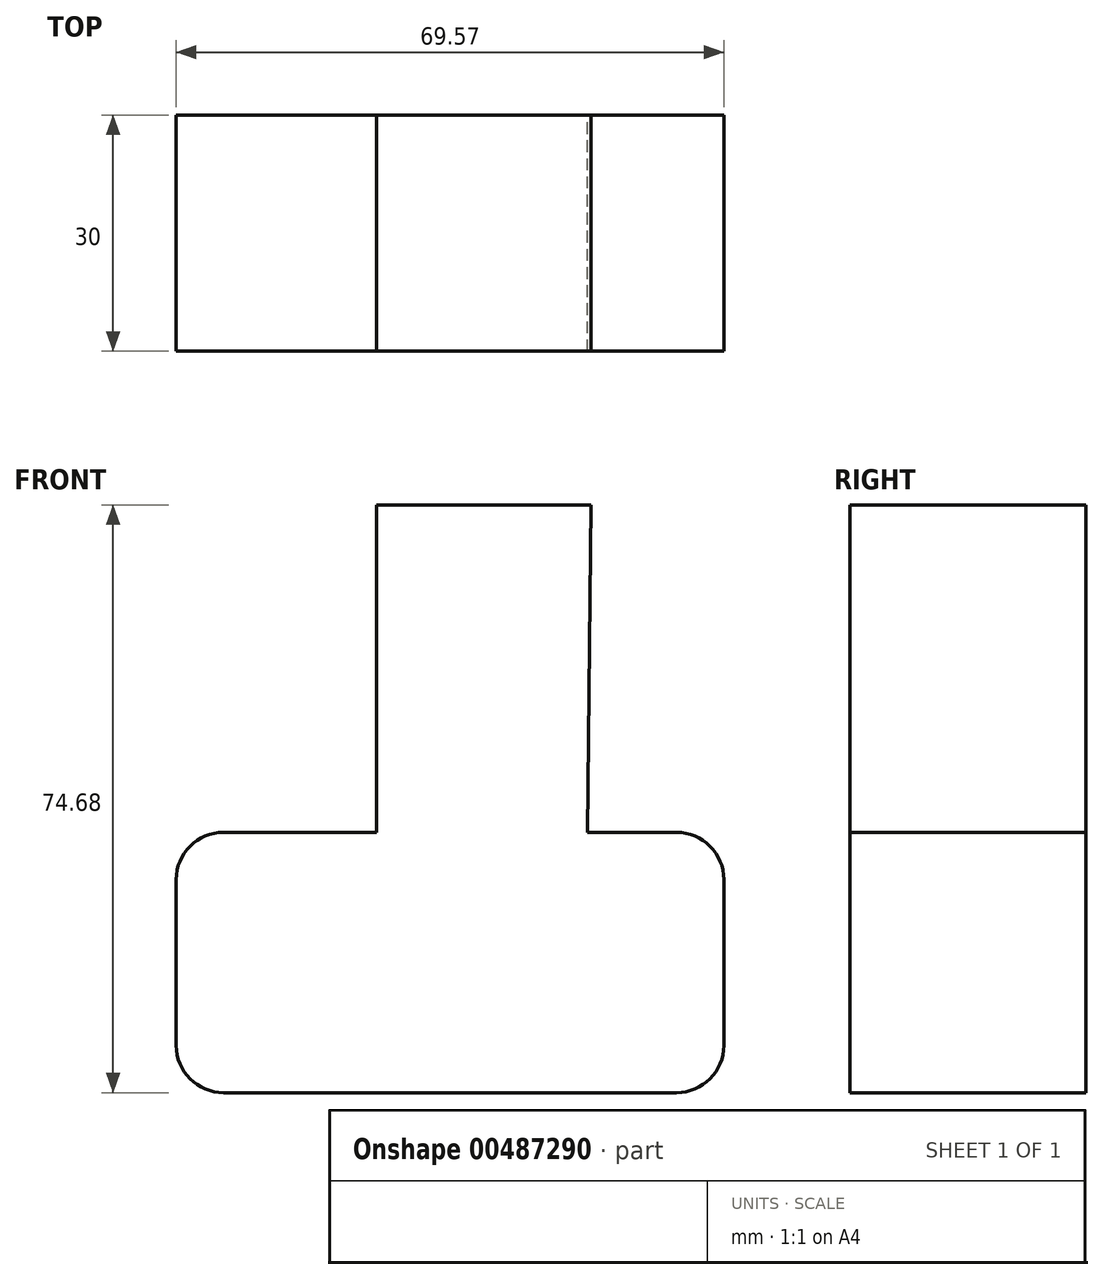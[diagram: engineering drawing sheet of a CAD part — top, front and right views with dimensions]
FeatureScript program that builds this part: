
annotation { "Feature Type Name" : "Feature", "Feature Type Description" : "" }
export const myFeature = defineFeature(function(context is Context, id is Id, definition is map)
    precondition{}
    {
        {
            var Q0;
            Q0=qCreatedBy(makeId("Front.planeOp"),FACE);
            var sketch = newSketch(context, id + "F0", { "sketchPlane" : qUnion([Q0])});
            skLineSegment(sketch, "E0", {"start": v(-14.74, -17.73) * mm, "end": v(42.83, -17.73) * mm});
            skLineSegment(sketch, "E1", {"start": v(48.83, -11.73) * mm, "end": v(48.83, 9.33) * mm});
            skLineSegment(sketch, "E2", {"start": v(42.83, 15.33) * mm, "end": v(-14.74, 15.33) * mm});
            skLineSegment(sketch, "E3", {"start": v(-20.74, 9.33) * mm, "end": v(-20.74, -11.73) * mm});
            skPoint(sketch, "E4.visualSharp", {"position": v(-20.74, 15.33) * mm});
            skArc(sketch, "E4.filletArc", {"start": v(-14.74, 15.33) * mm, "mid": v(-18.98, 13.58) * mm, "end": v(-20.74, 9.33) * mm});
            skPoint(sketch, "E5.visualSharp", {"position": v(-20.74, -17.73) * mm});
            skArc(sketch, "E5.filletArc", {"start": v(-20.74, -11.73) * mm, "mid": v(-18.98, -15.97) * mm, "end": v(-14.74, -17.73) * mm});
            skPoint(sketch, "E6.visualSharp", {"position": v(48.83, 15.33) * mm});
            skArc(sketch, "E6.filletArc", {"start": v(48.83, 9.33) * mm, "mid": v(47.07, 13.58) * mm, "end": v(42.83, 15.33) * mm});
            skPoint(sketch, "E7.visualSharp", {"position": v(48.83, -17.73) * mm});
            skArc(sketch, "E7.filletArc", {"start": v(42.83, -17.73) * mm, "mid": v(47.07, -15.97) * mm, "end": v(48.83, -11.73) * mm});
            skLineSegment(sketch, "E8", {"start": v(4.72, 15.33) * mm, "end": v(4.72, 56.95) * mm});
            skLineSegment(sketch, "E9", {"start": v(4.72, 56.95) * mm, "end": v(31.94, 56.95) * mm});
            skLineSegment(sketch, "E10", {"start": v(31.94, 56.95) * mm, "end": v(31.51, 15.33) * mm});
            skSolve(sketch);
        }
        {
            var Q0;
            Q0=makeQuery(id+"F0.imprint","IMPRINT",FACE,{"disambiguationData":[TD([[makeQuery(id+"F0.imprint","IMPRINT",EDGE,{"derivedFrom":sQuery(id+"F0.wireOp",EDGE,"E0")}),1.0]])]});
            var Q1;
            {var subQ0=sQuery(id+"F0.wireOp",EDGE,"E8");Q1=makeQuery(id+"F0.imprint","IMPRINT",FACE,{"disambiguationData":[TD([[makeQuery(id+"F0.imprint","IMPRINT",EDGE,{"derivedFrom":subQ0}),-1.0]])]});}
            extrude(context, id + "F1", {"entities" : qUnion([Q0, Q1]), "depth" : 30 * mm});
        }
    });
